annotation { "Feature Type Name" : "Feature", "Feature Type Description" : "" }
export const myFeature = defineFeature(function(context is Context, id is Id, definition is map)
    precondition{}
    {
        {
            var Q0;
            Q0=qCreatedBy(makeId("Top.planeOp"),FACE);
            var sketch = newSketch(context, id + "F0", { "sketchPlane" : qUnion([Q0])});
            skLineSegment(sketch, "E0.bottom", {"start": v(0, 0) * mm, "end": v(9.53, 0) * mm});
            skLineSegment(sketch, "E0.top", {"start": v(7.94, 19.05) * mm, "end": v(60.33, 19.05) * mm});
            skLineSegment(sketch, "E0.left", {"start": v(0, 0) * mm, "end": v(0, 11.11) * mm});
            skLineSegment(sketch, "E0.right", {"start": v(60.33, 12.7) * mm, "end": v(60.33, 19.05) * mm});
            skCircle(sketch, "E1", {"center": v(7.94, 11.11) * mm, "radius": 2.38 * mm});
            skArc(sketch, "E2", {"start": v(15.66, 10.31) * mm, "mid": v(13.48, 9.51) * mm, "end": v(12.12, 7.63) * mm});
            skPoint(sketch, "E3.visualSharp", {"position": v(0, 19.05) * mm});
            skArc(sketch, "E3.filletArc", {"start": v(7.94, 19.05) * mm, "mid": v(2.32, 16.73) * mm, "end": v(0, 11.11) * mm});
            skLineSegment(sketch, "E4", {"start": v(9.53, 0) * mm, "end": v(12.12, 7.63) * mm});
            skLineSegment(sketch, "E5", {"start": v(60.33, 12.7) * mm, "end": v(15.66, 10.31) * mm});
            skSolve(sketch);
        }
        {
            var Q0;
            Q0 = qSketchRegion(id + "F0", true);
            extrude(context, id + "F1", {"entities" : qUnion([Q0]), "depth" : 2.38 * mm, "offsetDistance" : 25.4 * mm});
        }
        {
            var Q0;
            Q0=makeQuery(id+"F1.opExtrude","SWEPT_FACE",FACE,{"disambiguationData":[OSD([sQuery(id+"F0.wireOp",EDGE,"E0.top")])]});
            var sketch = newSketch(context, id + "F2", { "sketchPlane" : qUnion([Q0])});
            skLineSegment(sketch, "E6", {"start": v(-45.24, 2.38) * mm, "end": v(-45.24, 0) * mm});
            skLineSegment(sketch, "E7", {"start": v(-45.24, 2.38) * mm, "end": v(-60.33, 2.38) * mm});
            skLineSegment(sketch, "E8", {"start": v(-60.33, 1.59) * mm, "end": v(-45.24, 2.38) * mm});
            skLineSegment(sketch, "E9", {"start": v(-60.33, 0.8) * mm, "end": v(-45.24, 0) * mm});
            skPoint(sketch, "E10.end.orphan", {"position": v(-60.33, 0) * mm});
            skLineSegment(sketch, "E11", {"start": v(-60.33, 1.59) * mm, "end": v(-60.33, 2.38) * mm});
            skLineSegment(sketch, "E12", {"start": v(-60.33, 0.8) * mm, "end": v(-60.33, 0) * mm});
            skLineSegment(sketch, "E13", {"start": v(-45.24, 0) * mm, "end": v(-60.33, 0.8) * mm});
            skSolve(sketch);
        }
        {
            var Q0;
            Q0 = qSketchRegion(id + "F2", true);
            var Q1;
            {var subQ0=sQuery(id+"F2.wireOp",EDGE,"E12");Q1=makeQuery(id+"F2.imprint","IMPRINT",FACE,{"disambiguationData":[TD([[makeQuery(id+"F2.imprint","IMPRINT",EDGE,{"derivedFrom":subQ0}),1.0]])]});}
            extrude(context, id + "F3", {"entities" : qUnion([Q0, Q1]), "operationType" : NewBodyOperationType.REMOVE, "oppositeDirection" : true, "depth" : 25.4 * mm, "offsetDistance" : 25.4 * mm});
        }
        {
            var Q0;
            Q0=makeQuery(id+"F1.opExtrude","SWEPT_FACE",FACE,{"disambiguationData":[OSD([sQuery(id+"F0.wireOp",EDGE,"E0.left")])]});
            var sketch = newSketch(context, id + "F4", { "sketchPlane" : qUnion([Q0])});
            skLineSegment(sketch, "E14", {"start": v(-7.94, 0) * mm, "end": v(-7.94, 2.38) * mm});
            skLineSegment(sketch, "E15", {"start": v(0, 0.8) * mm, "end": v(-7.94, 0) * mm});
            skLineSegment(sketch, "E16", {"start": v(0, 0) * mm, "end": v(0, 0.8) * mm});
            skLineSegment(sketch, "E17", {"start": v(0, 1.59) * mm, "end": v(-7.94, 2.38) * mm});
            skLineSegment(sketch, "E18", {"start": v(0, 2.38) * mm, "end": v(0, 1.59) * mm});
            skLineSegment(sketch, "E19", {"start": v(-7.94, 2.38) * mm, "end": v(0, 2.38) * mm});
            skLineSegment(sketch, "E20", {"start": v(0, 0) * mm, "end": v(-7.94, 0) * mm});
            skSolve(sketch);
        }
        {
            var Q0;
            Q0 = qSketchRegion(id + "F4", true);
            extrude(context, id + "F5", {"entities" : qUnion([Q0]), "operationType" : NewBodyOperationType.REMOVE, "oppositeDirection" : true, "depth" : 25.4 * mm, "offsetDistance" : 25.4 * mm});
        }
        {
            var Q0;
            Q0=makeQuery(id+"F1.opExtrude","CAP_FACE",FACE,{"disambiguationData":[OSD([sQuery(id+"F0.wireOp",EDGE,"E0.bottom"),sQuery(id+"F0.wireOp",EDGE,"E0.top"),sQuery(id+"F0.wireOp",EDGE,"E0.left"),sQuery(id+"F0.wireOp",EDGE,"E0.right"),sQuery(id+"F0.wireOp",EDGE,"E1"),sQuery(id+"F0.wireOp",EDGE,"E2"),sQuery(id+"F0.wireOp",EDGE,"E3.filletArc"),sQuery(id+"F0.wireOp",EDGE,"E4"),sQuery(id+"F0.wireOp",EDGE,"E5")])],"isStart":false});
            var sketch = newSketch(context, id + "F6", { "sketchPlane" : qUnion([Q0])});
            skText(sketch, "E21", { "text": "Jude Irons", "fontName": "OpenSans-Regular.ttf"});
            const initialGuessF6  = {"E21": [0.01361, 0.01247, 1, 0, 0.00269]};
            skSetInitialGuess(sketch, initialGuessF6);
            skSolve(sketch);
        }
        {
            var Q0;
            Q0 = qSketchRegion(id + "F6", true);
            extrude(context, id + "F7", {"entities" : qUnion([Q0]), "operationType" : NewBodyOperationType.REMOVE, "oppositeDirection" : true, "depth" : 0.5 * mm, "offsetDistance" : 25.4 * mm});
        }
    });